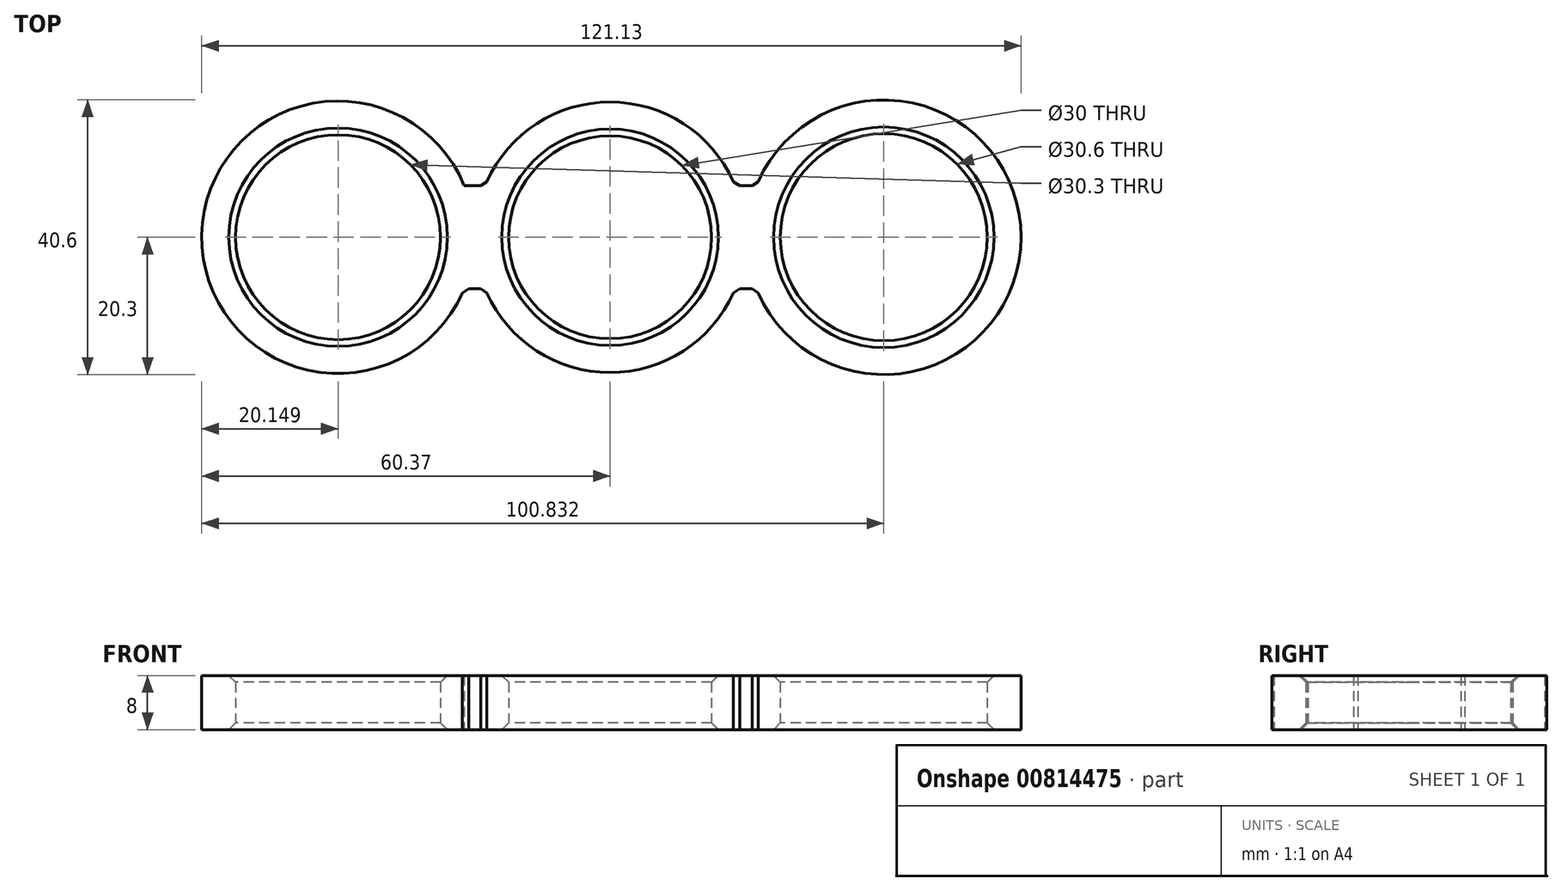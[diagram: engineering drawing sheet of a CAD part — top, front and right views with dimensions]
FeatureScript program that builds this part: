
annotation { "Feature Type Name" : "Feature", "Feature Type Description" : "" }
export const myFeature = defineFeature(function(context is Context, id is Id, definition is map)
    precondition{}
    {
        {
            var Q0;
            Q0=qCreatedBy(makeId("Top.planeOp"),FACE);
            var sketch = newSketch(context, id + "F0", { "sketchPlane" : qUnion([Q0])});
            skCircle(sketch, "E0", {"center": v(0, 0) * mm, "radius": 15 * mm});
            skCircle(sketch, "E1", {"center": v(0, 0) * mm, "radius": 20 * mm});
            skCircle(sketch, "E2", {"center": v(-40.22, 0) * mm, "radius": 15.15 * mm});
            skCircle(sketch, "E3.0", {"center": v(-40.22, 0) * mm, "radius": 20.15 * mm});
            skCircle(sketch, "E4", {"center": v(40.46, 0) * mm, "radius": 15.3 * mm});
            skCircle(sketch, "E5.0", {"center": v(40.46, 0) * mm, "radius": 20.3 * mm});
            skLineSegment(sketch, "E6.bottom", {"start": v(-27.14, 7.64) * mm, "end": v(27.14, 7.64) * mm});
            skLineSegment(sketch, "E6.top", {"start": v(-27.14, -7.64) * mm, "end": v(27.14, -7.64) * mm});
            skLineSegment(sketch, "E6.left", {"start": v(-27.14, 7.64) * mm, "end": v(-27.14, -7.64) * mm});
            skLineSegment(sketch, "E6.right", {"start": v(27.14, 7.64) * mm, "end": v(27.14, -7.64) * mm});
            skSolve(sketch);
        }
        {
            var Q0;
            Q0 = qSketchRegion(id + "F0", true);
            extrude(context, id + "F1", {"entities" : qUnion([Q0]), "depth" : 8 * mm, "offsetDistance" : 25 * mm});
        }
        {
            var Q0;
            Q0=makeQuery(id+"F1.opExtrude","CAP_EDGE",EDGE,{"disambiguationData":[OSD([sQuery(id+"F0.wireOp",EDGE,"E2")])],"isStart":false});
            var Q1;
            Q1=makeQuery(id+"F1.opExtrude","CAP_EDGE",EDGE,{"disambiguationData":[OSD([sQuery(id+"F0.wireOp",EDGE,"E0")])],"isStart":false});
            var Q2;
            Q2=makeQuery(id+"F1.opExtrude","CAP_EDGE",EDGE,{"disambiguationData":[OSD([sQuery(id+"F0.wireOp",EDGE,"E4")])],"isStart":false});
            var Q3;
            Q3=makeQuery(id+"F1.opExtrude","CAP_EDGE",EDGE,{"disambiguationData":[OSD([sQuery(id+"F0.wireOp",EDGE,"E2")])],"isStart":true});
            var Q4;
            Q4=makeQuery(id+"F1.opExtrude","CAP_EDGE",EDGE,{"disambiguationData":[OSD([sQuery(id+"F0.wireOp",EDGE,"E0")])],"isStart":true});
            var Q5;
            Q5=makeQuery(id+"F1.opExtrude","CAP_EDGE",EDGE,{"disambiguationData":[OSD([sQuery(id+"F0.wireOp",EDGE,"E4")])],"isStart":true});
            var Q6;
            Q6=makeQuery(id+"F1.opExtrude","SWEPT_EDGE",EDGE,{"disambiguationData":[OSD([sQuery(id+"F0.wireOp",EDGE,"E5.0"),sQuery(id+"F0.wireOp",EDGE,"E6.top")])]});
            var Q7;
            {var subQ0=sQuery(id+"F0.wireOp",EDGE,"E6.top");var subQ1=sQuery(id+"F0.wireOp",EDGE,"E1");Q7=makeQuery(id+"F1.opExtrude","SWEPT_EDGE",EDGE,{"disambiguationData":[OSD([subQ1,subQ0]),TDD([makeQuery(id+"F0.imprint","INTERSECT",VERTEX,{"disambiguationData":[OD(0.0)],"derivedFrom":[subQ1,subQ0]})])]});}
            var Q8;
            Q8=makeQuery(id+"F1.opExtrude","SWEPT_EDGE",EDGE,{"disambiguationData":[OSD([sQuery(id+"F0.wireOp",EDGE,"E5.0"),sQuery(id+"F0.wireOp",EDGE,"E6.bottom")])]});
            var Q9;
            {var subQ0=sQuery(id+"F0.wireOp",EDGE,"E6.bottom");var subQ1=sQuery(id+"F0.wireOp",EDGE,"E1");Q9=makeQuery(id+"F1.opExtrude","SWEPT_EDGE",EDGE,{"disambiguationData":[OSD([subQ1,subQ0]),TDD([makeQuery(id+"F0.imprint","INTERSECT",VERTEX,{"disambiguationData":[OD(1.0)],"derivedFrom":[subQ1,subQ0]})])]});}
            var Q10;
            {var subQ0=sQuery(id+"F0.wireOp",EDGE,"E6.bottom");var subQ1=sQuery(id+"F0.wireOp",EDGE,"E1");Q10=makeQuery(id+"F1.opExtrude","SWEPT_EDGE",EDGE,{"disambiguationData":[OSD([subQ1,subQ0]),TDD([makeQuery(id+"F0.imprint","INTERSECT",VERTEX,{"disambiguationData":[OD(0.0)],"derivedFrom":[subQ1,subQ0]})])]});}
            var Q11;
            {var subQ0=sQuery(id+"F0.wireOp",EDGE,"E6.top");var subQ1=sQuery(id+"F0.wireOp",EDGE,"E1");Q11=makeQuery(id+"F1.opExtrude","SWEPT_EDGE",EDGE,{"disambiguationData":[OSD([subQ1,subQ0]),TDD([makeQuery(id+"F0.imprint","INTERSECT",VERTEX,{"disambiguationData":[OD(1.0)],"derivedFrom":[subQ1,subQ0]})])]});}
            var Q12;
            Q12=makeQuery(id+"F1.opExtrude","SWEPT_EDGE",EDGE,{"disambiguationData":[OSD([sQuery(id+"F0.wireOp",EDGE,"E3.0"),sQuery(id+"F0.wireOp",EDGE,"E6.top")])]});
            chamfer(context, id + "F2", {"entities" : qUnion([Q0, Q1, Q2, Q3, Q4, Q5, Q6, Q7, Q8, Q9, Q10, Q11, Q12]), "width" : 1 * mm, "tangentPropagation" : true});
        }
    });
